# Revit family: CLARK ROUND DOUBLE TOWEL RAIL 600MM
name_source: partatom
category: Specialty Equipment
units: mm (PartAtom-declared; Revit-internal decimal feet)

## family parameters
Cut with Voids When Loaded = No
Host = Face
OmniClass Number = 23.40.20.21.27
OmniClass Title = Towel Bars
Part Type = Normal
Room Calculation Point = No
Round Connector Dimension = Use Radius
Shared = No

## types (2) — shared parameters
Assembly Code = C1030200
Default Elevation = 900 mm  [stored 2.95276 ft]
Manufacturer = GWA Bathrooms & Kitchens
Rail_Length = 600 mm
URL = https://www.clark.com.au

## per-type parameters (varying)
| type | Material_Base | Model |
| CLARK ROUND DOUBLE TOWEL RAIL 600MM - CHROME | GWA_Metal-Chrome | CL60033.C |
| CLARK ROUND DOUBLE TOWEL RAIL 600MM – MATTE BLACK | GWA-Metal-Black | CL60033.B |

note: column(s) folded — value = type name in every type: Description

note: [stored X ft] marks values corroborated as IEEE doubles in the binary element streams (Revit-internal decimal feet)

## geometry (parser evidence)
native form markers: Sweep x2
no freeform markers — native parametric forms only
